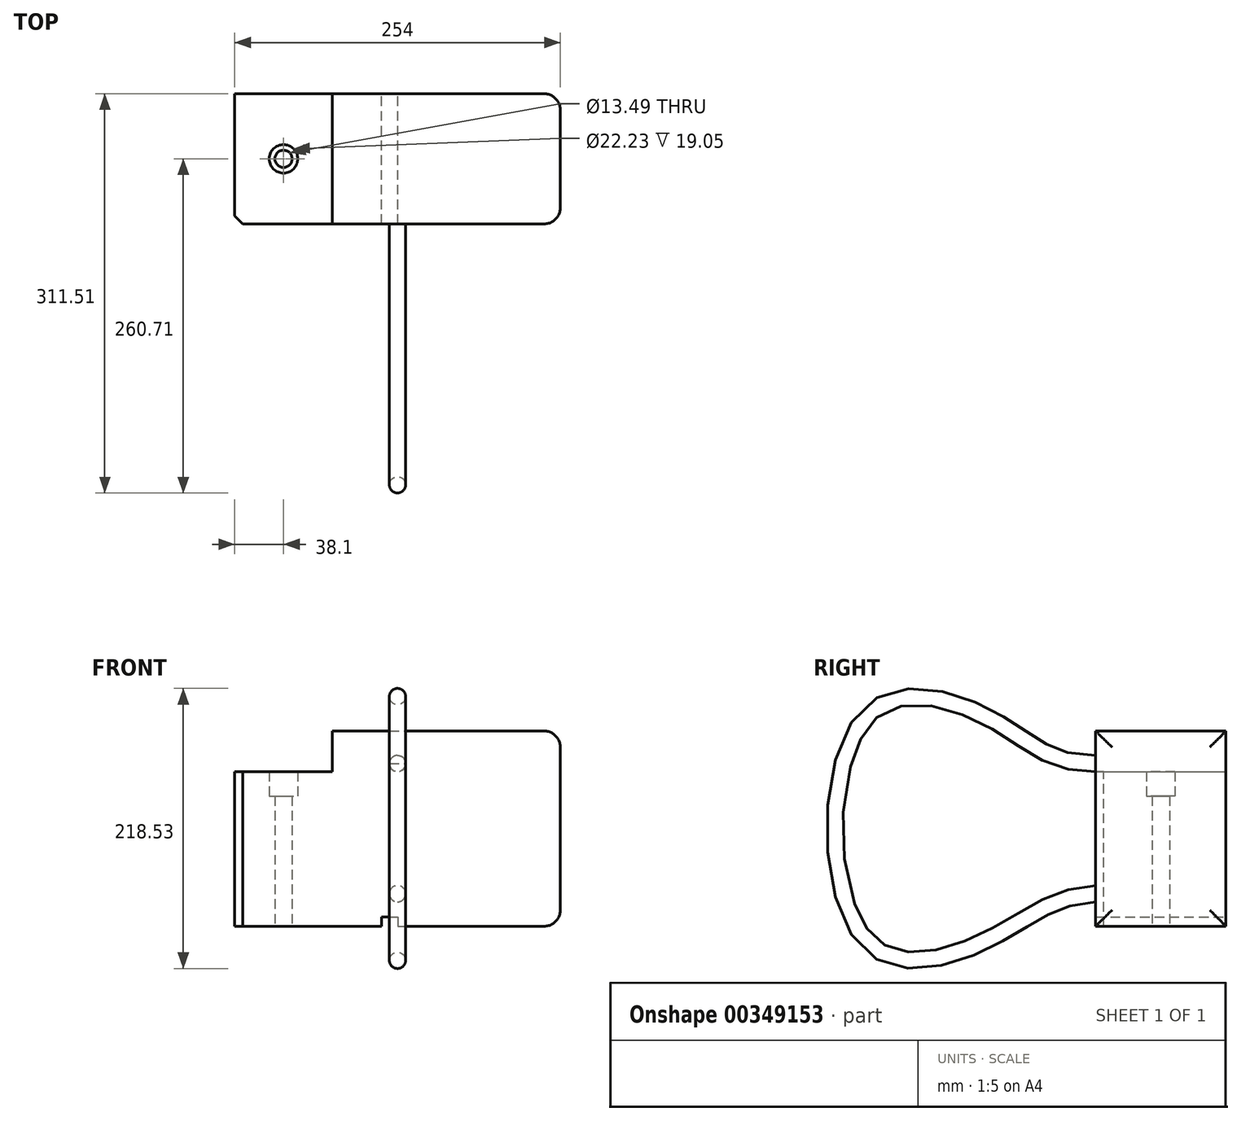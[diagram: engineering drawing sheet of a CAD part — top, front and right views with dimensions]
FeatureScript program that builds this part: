
annotation { "Feature Type Name" : "Feature", "Feature Type Description" : "" }
export const myFeature = defineFeature(function(context is Context, id is Id, definition is map)
    precondition{}
    {
        {
            var Q0;
            Q0=qCreatedBy(makeId("Front.planeOp"),FACE);
            var sketch = newSketch(context, id + "F0", { "sketchPlane" : qUnion([Q0])});
            skLineSegment(sketch, "E0.bottom", {"start": v(-50.8, 76.2) * mm, "end": v(127, 76.2) * mm});
            skLineSegment(sketch, "E0.top", {"start": v(-127, -76.2) * mm, "end": v(127, -76.2) * mm});
            skLineSegment(sketch, "E0.left", {"start": v(-127, 44.45) * mm, "end": v(-127, -76.2) * mm});
            skLineSegment(sketch, "E0.right", {"start": v(127, 76.2) * mm, "end": v(127, -76.2) * mm});
            skPoint(sketch, "E0.middle", {"position": v(0, 0) * mm});
            skLineSegment(sketch, "E1", {"start": v(-50.8, 76.2) * mm, "end": v(-50.8, 44.45) * mm});
            skLineSegment(sketch, "E2", {"start": v(-50.8, 44.45) * mm, "end": v(-127, 44.45) * mm});
            skPoint(sketch, "E3.orphan", {"position": v(-127, 76.2) * mm});
            skSolve(sketch);
        }
        {
            var Q0;
            Q0 = qSketchRegion(id + "F0", true);
            extrude(context, id + "F1", {"entities" : qUnion([Q0]), "depth" : 101.6 * mm, "symmetric" : true});
        }
        {
            var Q0;
            Q0=makeQuery(id+"F1.opExtrude","SWEPT_EDGE",EDGE,{"disambiguationData":[OSD([sQuery(id+"F0.wireOp",EDGE,"E0.bottom"),sQuery(id+"F0.wireOp",EDGE,"E0.right")])]});
            var Q1;
            Q1=makeQuery(id+"F1.opExtrude","CAP_EDGE",EDGE,{"disambiguationData":[OSD([sQuery(id+"F0.wireOp",EDGE,"E0.right")])],"isStart":false});
            var Q2;
            Q2=makeQuery(id+"F1.opExtrude","CAP_EDGE",EDGE,{"disambiguationData":[OSD([sQuery(id+"F0.wireOp",EDGE,"E0.right")])],"isStart":true});
            var Q3;
            Q3=makeQuery(id+"F1.opExtrude","SWEPT_EDGE",EDGE,{"disambiguationData":[OSD([sQuery(id+"F0.wireOp",EDGE,"E0.top"),sQuery(id+"F0.wireOp",EDGE,"E0.right")])]});
            fillet(context, id + "F2", {"entities" : qUnion([Q0, Q1, Q2, Q3]), "radius" : 12.7 * mm, "tangentPropagation" : true, "allowEdgeOverflow" : false});
        }
        {
            var Q0;
            Q0=makeQuery(id+"F1.opExtrude","SWEPT_FACE",FACE,{"disambiguationData":[OSD([sQuery(id+"F0.wireOp",EDGE,"E2")])]});
            var sketch = newSketch(context, id + "F3", { "sketchPlane" : qUnion([Q0])});
            skPoint(sketch, "E4", {"position": v(-88.9, 0) * mm});
            skSolve(sketch);
        }
        {
            var Q0;
            Q0=sQuery(id+"F3.wireOp",VERTEX,"E4");
            var Q1;
            Q1=makeQuery(id+"F1.opExtrude","SWEPT_BODY",BODY,{"disambiguationData":[OSD([sQuery(id+"F0.wireOp",EDGE,"E0.bottom"),sQuery(id+"F0.wireOp",EDGE,"E0.top"),sQuery(id+"F0.wireOp",EDGE,"E0.left"),sQuery(id+"F0.wireOp",EDGE,"E0.right"),sQuery(id+"F0.wireOp",EDGE,"E1"),sQuery(id+"F0.wireOp",EDGE,"E2")])]});
            hole(context, id + "F4", {"style" : HoleStyle.C_BORE, "endStyle" : HoleEndStyle.THROUGH, "holeDiameter" : 13.5 * mm, "cBoreDiameter" : 22.22 * mm, "cBoreDepth" : 19.05 * mm, "isTappedThrough" : true, "tappedDepth" : 12.7 * mm, "tapClearance" : 3, "locations" : qUnion([Q0]), "scope" : qUnion([Q1]), "startStyle" : HoleStartStyle.PART});
        }
        {
            var Q0;
            Q0=makeQuery(id+"F1.opExtrude","SWEPT_FACE",FACE,{"disambiguationData":[OSD([sQuery(id+"F0.wireOp",EDGE,"E0.top")])]});
            var sketch = newSketch(context, id + "F5", { "sketchPlane" : qUnion([Q0])});
            skLineSegment(sketch, "E5.bottom", {"start": v(-12.3, 50.8) * mm, "end": v(0.4, 50.8) * mm});
            skLineSegment(sketch, "E5.left", {"start": v(-12.3, 50.8) * mm, "end": v(-12.3, -50.8) * mm});
            skLineSegment(sketch, "E5.right", {"start": v(0.4, 50.8) * mm, "end": v(0.4, -50.8) * mm});
            skLineSegment(sketch, "E6", {"start": v(-12.3, -50.8) * mm, "end": v(0.4, -50.8) * mm});
            skSolve(sketch);
        }
        {
            var Q0;
            Q0=makeQuery(id+"F5.imprint","IMPRINT",FACE,{"disambiguationData":[TD([[makeQuery(id+"F5.imprint","IMPRINT",EDGE,{"derivedFrom":sQuery(id+"F5.wireOp",EDGE,"E5.bottom")}),-1.0]])]});
            extrude(context, id + "F6", {"entities" : qUnion([Q0]), "operationType" : NewBodyOperationType.REMOVE, "oppositeDirection" : true, "depth" : 7.14 * mm});
        }
        {
            var Q0;
            Q0=qCreatedBy(makeId("Right.planeOp"),FACE);
            var sketch = newSketch(context, id + "F7", { "sketchPlane" : qUnion([Q0])});
            skFitSpline(sketch, "E7", {"points": [v(-50.8, 50.8) * mm, v(-127, 82.55) * mm, v(-228.6, 88.9) * mm, v(-228.6, -88.9) * mm, v(-127, -82.55) * mm, v(-50.8, -50.8) * mm], "startDerivative": vector(-634.85, -9.52) * mm, "endDerivative": vector(561.44, 23.16) * mm});
            skSolve(sketch);
        }
        {
            var Q0;
            Q0=makeQuery(id+"F1.opExtrude","CAP_FACE",FACE,{"disambiguationData":[OSD([sQuery(id+"F0.wireOp",EDGE,"E0.bottom"),sQuery(id+"F0.wireOp",EDGE,"E0.top"),sQuery(id+"F0.wireOp",EDGE,"E0.left"),sQuery(id+"F0.wireOp",EDGE,"E0.right"),sQuery(id+"F0.wireOp",EDGE,"E1"),sQuery(id+"F0.wireOp",EDGE,"E2")])],"isStart":false});
            var sketch = newSketch(context, id + "F8", { "sketchPlane" : qUnion([Q0])});
            skCircle(sketch, "E8", {"center": v(0, -50.8) * mm, "radius": 6.35 * mm});
            skSolve(sketch);
        }
        {
            var Q0;
            Q0 = qSketchRegion(id + "F8", true);
            var Q1;
            Q1 = qConstructionFilter(qBodyType(qCreatedBy(id + "F7" ,EDGE), BodyType.WIRE), ConstructionObject.NO);
            sweep(context, id + "F9", {"operationType" : NewBodyOperationType.ADD, "profiles" : qUnion([Q0]), "path" : qUnion([Q1])});
        }
        {
            var Q0;
            Q0=makeQuery(id+"F1.opExtrude","CAP_EDGE",EDGE,{"disambiguationData":[OSD([sQuery(id+"F0.wireOp",EDGE,"E0.left")])],"isStart":false});
            chamfer(context, id + "F10", {"entities" : qUnion([Q0]), "width" : 6.35 * mm, "tangentPropagation" : true});
        }
    });
